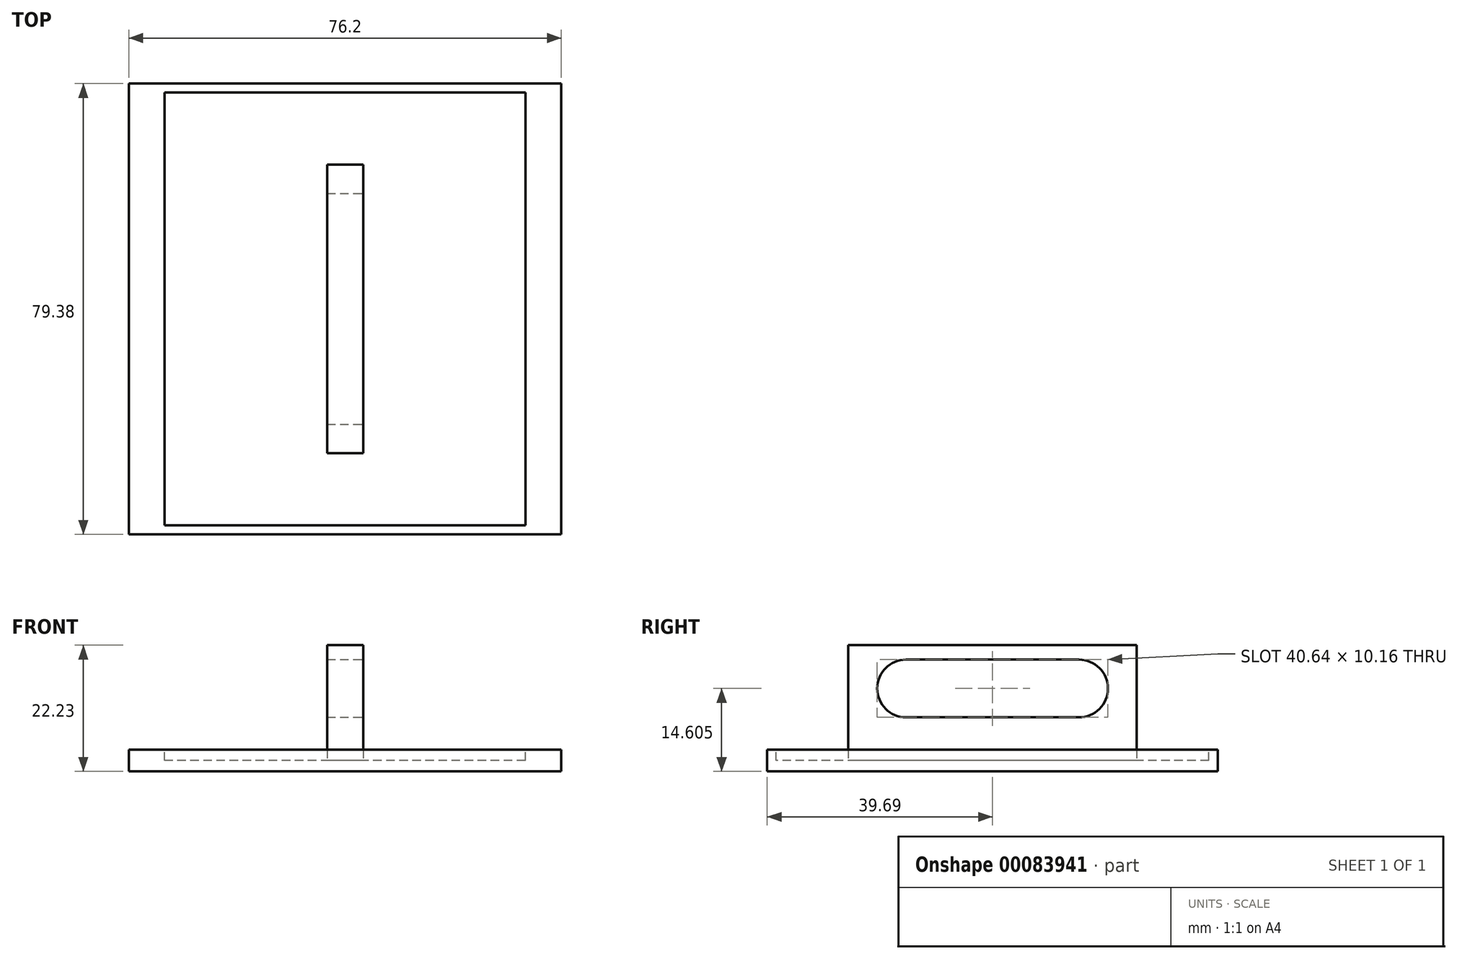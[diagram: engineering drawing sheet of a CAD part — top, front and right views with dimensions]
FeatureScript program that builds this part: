
annotation { "Feature Type Name" : "Feature", "Feature Type Description" : "" }
export const myFeature = defineFeature(function(context is Context, id is Id, definition is map)
    precondition{}
    {
        {
            var Q0;
            Q0=qCreatedBy(makeId("Top.planeOp"),FACE);
            var sketch = newSketch(context, id + "F0", { "sketchPlane" : qUnion([Q0])});
            skLineSegment(sketch, "E0.bottom", {"start": v(38.1, 39.69) * mm, "end": v(-38.1, 39.69) * mm});
            skLineSegment(sketch, "E0.top", {"start": v(38.1, -39.69) * mm, "end": v(-38.1, -39.69) * mm});
            skLineSegment(sketch, "E0.left", {"start": v(38.1, 39.69) * mm, "end": v(38.1, -39.69) * mm});
            skLineSegment(sketch, "E0.right", {"start": v(-38.1, 39.69) * mm, "end": v(-38.1, -39.69) * mm});
            skPoint(sketch, "E0.middle", {"position": v(0, 0) * mm});
            skSolve(sketch);
        }
        {
            var Q0;
            Q0 = qSketchRegion(id + "F0", true);
            extrude(context, id + "F1", {"entities" : qUnion([Q0]), "depth" : 3.8 * mm});
        }
        {
            var Q0;
            Q0=makeQuery(id+"F1.opExtrude","CAP_FACE",FACE,{"disambiguationData":[OSD([sQuery(id+"F0.wireOp",EDGE,"E0.bottom"),sQuery(id+"F0.wireOp",EDGE,"E0.top"),sQuery(id+"F0.wireOp",EDGE,"E0.left"),sQuery(id+"F0.wireOp",EDGE,"E0.right")])],"isStart":false});
            var sketch = newSketch(context, id + "F2", { "sketchPlane" : qUnion([Q0])});
            skLineSegment(sketch, "E1.bottom", {"start": v(31.75, 38.1) * mm, "end": v(-31.75, 38.1) * mm});
            skLineSegment(sketch, "E1.top", {"start": v(31.75, -38.1) * mm, "end": v(-31.75, -38.1) * mm});
            skLineSegment(sketch, "E1.left", {"start": v(31.75, 38.1) * mm, "end": v(31.75, -38.1) * mm});
            skLineSegment(sketch, "E1.right", {"start": v(-31.75, 38.1) * mm, "end": v(-31.75, -38.1) * mm});
            skPoint(sketch, "E1.middle", {"position": v(0, 0) * mm});
            skSolve(sketch);
        }
        {
            var Q0;
            Q0 = qSketchRegion(id + "F2", true);
            extrude(context, id + "F3", {"entities" : qUnion([Q0]), "operationType" : NewBodyOperationType.REMOVE, "oppositeDirection" : true, "depth" : 1.9 * mm});
        }
        {
            var Q0;
            Q0=makeQuery(id+"F3.boolean.opBoolean","COPY",FACE,{"derivedFrom":makeQuery(id+"F3.opExtrude","CAP_FACE",FACE,{"disambiguationData":[OSD([sQuery(id+"F2.wireOp",EDGE,"E1.bottom"),sQuery(id+"F2.wireOp",EDGE,"E1.top"),sQuery(id+"F2.wireOp",EDGE,"E1.left"),sQuery(id+"F2.wireOp",EDGE,"E1.right")])],"isStart":false})});
            var sketch = newSketch(context, id + "F4", { "sketchPlane" : qUnion([Q0])});
            skLineSegment(sketch, "E2.bottom", {"start": v(3.18, 25.4) * mm, "end": v(-3.17, 25.4) * mm});
            skLineSegment(sketch, "E2.top", {"start": v(3.17, -25.4) * mm, "end": v(-3.18, -25.4) * mm});
            skLineSegment(sketch, "E2.left", {"start": v(3.18, 25.4) * mm, "end": v(3.17, -25.4) * mm});
            skLineSegment(sketch, "E2.right", {"start": v(-3.17, 25.4) * mm, "end": v(-3.18, -25.4) * mm});
            skPoint(sketch, "E2.middle", {"position": v(0, 0) * mm});
            skSolve(sketch);
        }
        {
            var Q0;
            Q0 = qSketchRegion(id + "F4", true);
            extrude(context, id + "F5", {"entities" : qUnion([Q0]), "operationType" : NewBodyOperationType.ADD, "depth" : 25.4 * mm});
        }
        {
            var Q0;
            Q0=makeQuery(id+"F5.opExtrude","SWEPT_FACE",FACE,{"disambiguationData":[OSD([sQuery(id+"F4.wireOp",EDGE,"E2.left")])]});
            var sketch = newSketch(context, id + "F6", { "sketchPlane" : qUnion([Q0])});
            skLineSegment(sketch, "E3.bottom", {"start": v(15.24, 19.69) * mm, "end": v(-15.24, 19.69) * mm});
            skLineSegment(sketch, "E3.top", {"start": v(15.24, 9.53) * mm, "end": v(-15.24, 9.53) * mm});
            skPoint(sketch, "E3.middle", {"position": v(0, 14.6) * mm});
            skPoint(sketch, "E3.middle.positionSnap0", {"position": v(-25.4, 14.6) * mm});
            skPoint(sketch, "E3.middle.positionSnap1", {"position": v(0, 27.3) * mm});
            skPoint(sketch, "E3.centerSnap0", {"position": v(-25.4, 14.6) * mm});
            skPoint(sketch, "E3.centerSnap1", {"position": v(0, 27.3) * mm});
            skArc(sketch, "E4", {"start": v(-15.24, 19.69) * mm, "mid": v(-20.32, 14.6) * mm, "end": v(-15.24, 9.53) * mm});
            skArc(sketch, "E5", {"start": v(15.24, 9.53) * mm, "mid": v(20.32, 14.6) * mm, "end": v(15.24, 19.69) * mm});
            skSolve(sketch);
        }
        {
            var Q0;
            Q0 = qSketchRegion(id + "F6", true);
            extrude(context, id + "F7", {"entities" : qUnion([Q0]), "operationType" : NewBodyOperationType.REMOVE, "oppositeDirection" : true, "depth" : 25.4 * mm});
        }
        {
            var Q0;
            Q0=makeQuery(id+"F5.opExtrude","SWEPT_FACE",FACE,{"disambiguationData":[OSD([sQuery(id+"F4.wireOp",EDGE,"E2.left")])]});
            var sketch = newSketch(context, id + "F8", { "sketchPlane" : qUnion([Q0])});
            skLineSegment(sketch, "E6.bottom", {"start": v(-25.4, 27.3) * mm, "end": v(25.4, 27.3) * mm});
            skLineSegment(sketch, "E6.top", {"start": v(-25.4, 22.23) * mm, "end": v(25.4, 22.23) * mm});
            skLineSegment(sketch, "E6.left", {"start": v(-25.4, 27.3) * mm, "end": v(-25.4, 22.23) * mm});
            skLineSegment(sketch, "E6.right", {"start": v(25.4, 27.3) * mm, "end": v(25.4, 22.23) * mm});
            skSolve(sketch);
        }
        {
            var Q0;
            Q0 = qSketchRegion(id + "F8", true);
            extrude(context, id + "F9", {"entities" : qUnion([Q0]), "operationType" : NewBodyOperationType.REMOVE, "oppositeDirection" : true, "depth" : 25.4 * mm});
        }
    });
